FCSTD DOCUMENT  (FreeCAD 0.19R24291 (Git))
Label: front_panel
License: All rights reserved
LicenseURL: http://en.wikipedia.org/wiki/All_rights_reserved
objects: Sketcher::SketchObject×3, PartDesign::Body×1
note: 4 computed .brp shape members not serialized (recipe doc carries the construction recipe); baked Part::Feature solids carry a one-line shape summary decoded from their .brp

FEATURE [Sketcher::SketchObject] Sketch  label="Reference"
  FullyConstrained = true
  MapMode = 5
  Support = -> [XY_Plane]
  sketch-geometry (89):
    g0: Circle CenterX=-179 CenterY=-83 CenterZ=0 NormalX=0 NormalY=0 NormalZ=1 AngleXU=0 Radius=1.85
    g1: Circle CenterX=-89 CenterY=-83 CenterZ=0 NormalX=0 NormalY=0 NormalZ=1 AngleXU=0 Radius=1.85
    g2: Circle CenterX=0 CenterY=-83 CenterZ=0 NormalX=0 NormalY=0 NormalZ=1 AngleXU=0 Radius=1.85
    g3: Circle CenterX=89 CenterY=-83 CenterZ=0 NormalX=0 NormalY=0 NormalZ=1 AngleXU=0 Radius=1.85
    g4: Circle CenterX=179 CenterY=-83 CenterZ=0 NormalX=0 NormalY=0 NormalZ=1 AngleXU=0 Radius=1.85
    g5: Circle CenterX=-179 CenterY=83 CenterZ=0 NormalX=0 NormalY=0 NormalZ=1 AngleXU=0 Radius=1.85
    g6: Circle CenterX=-89 CenterY=83 CenterZ=0 NormalX=0 NormalY=0 NormalZ=1 AngleXU=0 Radius=1.85
    g7: Circle CenterX=0 CenterY=83 CenterZ=0 NormalX=0 NormalY=0 NormalZ=1 AngleXU=0 Radius=1.85
    g8: Circle CenterX=89 CenterY=83 CenterZ=0 NormalX=0 NormalY=0 NormalZ=1 AngleXU=0 Radius=1.85
    g9: Circle CenterX=179 CenterY=83 CenterZ=0 NormalX=0 NormalY=0 NormalZ=1 AngleXU=0 Radius=1.85
    g10: LineSegment StartX=-185 StartY=75.75 StartZ=0 EndX=185 EndY=75.75 EndZ=0
    g11: LineSegment StartX=185 StartY=75.75 StartZ=0 EndX=185 EndY=-75.75 EndZ=0
    g12: LineSegment StartX=185 StartY=-75.75 StartZ=0 EndX=-185 EndY=-75.75 EndZ=0
    g13: LineSegment StartX=-185 StartY=-75.75 StartZ=0 EndX=-185 EndY=75.75 EndZ=0
    g14: LineSegment StartX=-185 StartY=75.75 StartZ=0 EndX=-175 EndY=75.75 EndZ=0
    g15: LineSegment StartX=-175 StartY=75.75 StartZ=0 EndX=-175 EndY=86.75 EndZ=0
    g16: LineSegment StartX=-175 StartY=86.75 StartZ=0 EndX=-185 EndY=86.75 EndZ=0
    g17: LineSegment StartX=-185 StartY=86.75 StartZ=0 EndX=-185 EndY=75.75 EndZ=0
    g18: LineSegment StartX=-185 StartY=56.25 StartZ=0 EndX=185 EndY=56.25 EndZ=0
    g19: LineSegment StartX=-185 StartY=-56.25 StartZ=0 EndX=185 EndY=-56.25 EndZ=0
    g20: LineSegment StartX=-165.5 StartY=55.5 StartZ=0 EndX=-162.5 EndY=55.5 EndZ=0
    g21: LineSegment StartX=-162.5 StartY=55.5 StartZ=0 EndX=-162.5 EndY=-55.5 EndZ=0
    g22: LineSegment StartX=-162.5 StartY=-55.5 StartZ=0 EndX=-165.5 EndY=-55.5 EndZ=0
    g23: LineSegment StartX=-165.5 StartY=-55.5 StartZ=0 EndX=-165.5 EndY=55.5 EndZ=0
    g24: GeomPoint X=-164 Y=55.5 Z=0
    g25: LineSegment StartX=-144.5 StartY=55.5 StartZ=0 EndX=-141.5 EndY=55.5 EndZ=0
    g26: LineSegment StartX=-141.5 StartY=55.5 StartZ=0 EndX=-141.5 EndY=-55.5 EndZ=0
    g27: LineSegment StartX=-141.5 StartY=-55.5 StartZ=0 EndX=-144.5 EndY=-55.5 EndZ=0
    g28: LineSegment StartX=-144.5 StartY=-55.5 StartZ=0 EndX=-144.5 EndY=55.5 EndZ=0
    g29: LineSegment StartX=-123.5 StartY=-55.5 StartZ=0 EndX=-120.5 EndY=-55.5 EndZ=0
    g30: LineSegment StartX=-120.5 StartY=-55.5 StartZ=0 EndX=-120.5 EndY=55.5 EndZ=0
    g31: LineSegment StartX=-120.5 StartY=55.5 StartZ=0 EndX=-123.5 EndY=55.5 EndZ=0
    g32: LineSegment StartX=-123.5 StartY=55.5 StartZ=0 EndX=-123.5 EndY=-55.5 EndZ=0
    g33: LineSegment StartX=-102.5 StartY=-55.5 StartZ=0 EndX=-99.5 EndY=-55.5 EndZ=0
    g34: LineSegment StartX=-99.5 StartY=-55.5 StartZ=0 EndX=-99.5 EndY=55.5 EndZ=0
    g35: LineSegment StartX=-99.5 StartY=55.5 StartZ=0 EndX=-102.5 EndY=55.5 EndZ=0
    g36: LineSegment StartX=-102.5 StartY=55.5 StartZ=0 EndX=-102.5 EndY=-55.5 EndZ=0
    g37: LineSegment StartX=-81.5 StartY=-55.5 StartZ=0 EndX=-78.5 EndY=-55.5 EndZ=0
    g38: LineSegment StartX=-78.5 StartY=-55.5 StartZ=0 EndX=-78.5 EndY=55.5 EndZ=0
    g39: LineSegment StartX=-78.5 StartY=55.5 StartZ=0 EndX=-81.5 EndY=55.5 EndZ=0
    g40: LineSegment StartX=-81.5 StartY=55.5 StartZ=0 EndX=-81.5 EndY=-55.5 EndZ=0
    g41: LineSegment StartX=-60.5 StartY=-55.5 StartZ=0 EndX=-57.5 EndY=-55.5 EndZ=0
    g42: LineSegment StartX=-57.5 StartY=-55.5 StartZ=0 EndX=-57.5 EndY=55.5 EndZ=0
    g43: LineSegment StartX=-57.5 StartY=55.5 StartZ=0 EndX=-60.5 EndY=55.5 EndZ=0
    g44: LineSegment StartX=-60.5 StartY=55.5 StartZ=0 EndX=-60.5 EndY=-55.5 EndZ=0
    g45: LineSegment StartX=-39.5 StartY=-55.5 StartZ=0 EndX=-36.5 EndY=-55.5 EndZ=0
    g46: LineSegment StartX=-36.5 StartY=-55.5 StartZ=0 EndX=-36.5 EndY=55.5 EndZ=0
    g47: LineSegment StartX=-36.5 StartY=55.5 StartZ=0 EndX=-39.5 EndY=55.5 EndZ=0
    g48: LineSegment StartX=-39.5 StartY=55.5 StartZ=0 EndX=-39.5 EndY=-55.5 EndZ=0
    g49: LineSegment StartX=-18.5 StartY=55.5 StartZ=0 EndX=-15.5 EndY=55.5 EndZ=0
    g50: LineSegment StartX=-15.5 StartY=55.5 StartZ=0 EndX=-15.5 EndY=-55.5 EndZ=0
    g51: LineSegment StartX=-15.5 StartY=-55.5 StartZ=0 EndX=-18.5 EndY=-55.5 EndZ=0
    g52: LineSegment StartX=-18.5 StartY=-55.5 StartZ=0 EndX=-18.5 EndY=55.5 EndZ=0
    g53: LineSegment StartX=2.5 StartY=55.5 StartZ=0 EndX=5.5 EndY=55.5 EndZ=0
    g54: LineSegment StartX=5.5 StartY=55.5 StartZ=0 EndX=5.5 EndY=-55.5 EndZ=0
    g55: LineSegment StartX=5.5 StartY=-55.5 StartZ=0 EndX=2.5 EndY=-55.5 EndZ=0
    g56: LineSegment StartX=2.5 StartY=-55.5 StartZ=0 EndX=2.5 EndY=55.5 EndZ=0
    g57: LineSegment StartX=23.5 StartY=55.5 StartZ=0 EndX=26.5 EndY=55.5 EndZ=0
    g58: LineSegment StartX=26.5 StartY=55.5 StartZ=0 EndX=26.5 EndY=-55.5 EndZ=0
    g59: LineSegment StartX=26.5 StartY=-55.5 StartZ=0 EndX=23.5 EndY=-55.5 EndZ=0
    g60: LineSegment StartX=23.5 StartY=-55.5 StartZ=0 EndX=23.5 EndY=55.5 EndZ=0
    g61: LineSegment StartX=44.5 StartY=55.5 StartZ=0 EndX=47.5 EndY=55.5 EndZ=0
    g62: LineSegment StartX=47.5 StartY=55.5 StartZ=0 EndX=47.5 EndY=-55.5 EndZ=0
    g63: LineSegment StartX=47.5 StartY=-55.5 StartZ=0 EndX=44.5 EndY=-55.5 EndZ=0
    g64: LineSegment StartX=44.5 StartY=-55.5 StartZ=0 EndX=44.5 EndY=55.5 EndZ=0
    g65: LineSegment StartX=65.5 StartY=55.5 StartZ=0 EndX=68.5 EndY=55.5 EndZ=0
    g66: LineSegment StartX=68.5 StartY=55.5 StartZ=0 EndX=68.5 EndY=-55.5 EndZ=0
    g67: LineSegment StartX=68.5 StartY=-55.5 StartZ=0 EndX=65.5 EndY=-55.5 EndZ=0
    g68: LineSegment StartX=65.5 StartY=-55.5 StartZ=0 EndX=65.5 EndY=55.5 EndZ=0
    g69: LineSegment StartX=86.5 StartY=55.5 StartZ=0 EndX=89.5 EndY=55.5 EndZ=0
    g70: LineSegment StartX=89.5 StartY=55.5 StartZ=0 EndX=89.5 EndY=-55.5 EndZ=0
    g71: LineSegment StartX=89.5 StartY=-55.5 StartZ=0 EndX=86.5 EndY=-55.5 EndZ=0
    g72: LineSegment StartX=86.5 StartY=-55.5 StartZ=0 EndX=86.5 EndY=55.5 EndZ=0
    g73: LineSegment StartX=107.5 StartY=55.5 StartZ=0 EndX=110.5 EndY=55.5 EndZ=0
    g74: LineSegment StartX=110.5 StartY=55.5 StartZ=0 EndX=110.5 EndY=-55.5 EndZ=0
    g75: LineSegment StartX=110.5 StartY=-55.5 StartZ=0 EndX=107.5 EndY=-55.5 EndZ=0
    g76: LineSegment StartX=107.5 StartY=-55.5 StartZ=0 EndX=107.5 EndY=55.5 EndZ=0
    g77: LineSegment StartX=128.5 StartY=55.5 StartZ=0 EndX=131.5 EndY=55.5 EndZ=0
    g78: LineSegment StartX=131.5 StartY=55.5 StartZ=0 EndX=131.5 EndY=-55.5 EndZ=0
    g79: LineSegment StartX=131.5 StartY=-55.5 StartZ=0 EndX=128.5 EndY=-55.5 EndZ=0
    g80: LineSegment StartX=128.5 StartY=-55.5 StartZ=0 EndX=128.5 EndY=55.5 EndZ=0
    g81: LineSegment StartX=149.5 StartY=55.5 StartZ=0 EndX=152.5 EndY=55.5 EndZ=0
    g82: LineSegment StartX=152.5 StartY=55.5 StartZ=0 EndX=152.5 EndY=-55.5 EndZ=0
    g83: LineSegment StartX=152.5 StartY=-55.5 StartZ=0 EndX=149.5 EndY=-55.5 EndZ=0
    g84: LineSegment StartX=149.5 StartY=-55.5 StartZ=0 EndX=149.5 EndY=55.5 EndZ=0
    g85: LineSegment StartX=175.5 StartY=55.5 StartZ=0 EndX=178.5 EndY=55.5 EndZ=0
    g86: LineSegment StartX=178.5 StartY=55.5 StartZ=0 EndX=178.5 EndY=-55.5 EndZ=0
    g87: LineSegment StartX=178.5 StartY=-55.5 StartZ=0 EndX=175.5 EndY=-55.5 EndZ=0
    g88: LineSegment StartX=175.5 StartY=-55.5 StartZ=0 EndX=175.5 EndY=55.5 EndZ=0
  constraints (256):
    c: PointOnObject(g2,g-2)
    c: Horizontal(g0,g1)
    c: Horizontal(g1,g2)
    c: Symmetric(g1,g3,g-2)
    c: Symmetric(g0,g4,g-2)
    c: DistanceX(g1,g2) = 89
    c: DistanceX(g0,g1) = 90
    c: Equal(g0,g1)
    c: Equal(g1,g2)
    c: Equal(g2,g3)
    c: Equal(g3,g4)
    c: Diameter(g0) = 3.7
    c: Equal(g5,g6)
    c: Equal(g6,g8)
    c: Equal(g8,g9)
    c: Equal(g9,g7)
    c: Equal(g7,g0)
    c: Symmetric(g5,g0,g-1)
    c: Symmetric(g6,g1,g-1)
    c: Symmetric(g7,g2,g-1)
    c: Symmetric(g8,g3,g-1)
    c: Symmetric(g9,g4,g-1)
    c: Coincident(g10,g11)
    c: Coincident(g11,g12)
    c: Coincident(g12,g13)
    c: Coincident(g13,g10)
    c: Horizontal(g10)
    c: Horizontal(g12)
    c: Vertical(g11)
    c: Vertical(g13)
    c: DistanceY(g11,g11) = 151.5
    c: Symmetric(g10,g11,g-1)
    c: DistanceY(g10,g5) = 7.25
    c: Coincident(g14,g15)
    c: Coincident(g15,g16)
    c: Coincident(g16,g17)
    c: Coincident(g17,g14)
    c: Horizontal(g14)
    c: Horizontal(g16)
    c: Vertical(g15)
    c: Vertical(g17)
    c: Coincident(g14,g10)
    c: DistanceY(g15,g15) = 11
    c: DistanceX(g16,g16) = 10
    c: PointOnObject(g18,g13)
    c: PointOnObject(g18,g11)
    c: Horizontal(g18)
    c: PointOnObject(g19,g13)
    c: Horizontal(g19)
    c: Symmetric(g18,g19,g-1)
    c: DistanceY(g19,g18) = 112.5
    c: Coincident(g20,g21)
    c: Coincident(g21,g22)
    c: Coincident(g22,g23)
    c: Coincident(g23,g20)
    c: Horizontal(g20)
    c: Horizontal(g22)
    c: Vertical(g23)
    c: Symmetric(g20,g21,g-1)
    c: DistanceY(g23,g23) = 111
    c: DistanceX(g20,g20) = 3
    c: Symmetric(g20,g20,g24)
    c: DistanceX(g18,g24) = 21
    c: Coincident(g25,g26)
    c: Coincident(g26,g27)
    c: Coincident(g27,g28)
    c: Coincident(g28,g25)
    c: Horizontal(g25)
    c: Horizontal(g27)
    c: Vertical(g26)
    c: Vertical(g28)
    c: DistanceX(g20,g25) = 21
    c: Equal(g25,g20)
    c: Equal(g28,g23)
    c: Horizontal(g20,g25)
    c: Coincident(g29,g30)
    c: Coincident(g30,g31)
    c: Coincident(g31,g32)
    c: Coincident(g32,g29)
    c: Horizontal(g29)
    c: Horizontal(g31)
    c: Vertical(g30)
    c: Vertical(g32)
    c: Coincident(g33,g34)
    c: Coincident(g34,g35)
    c: Coincident(g35,g36)
    c: Coincident(g36,g33)
    c: Horizontal(g33)
    c: Horizontal(g35)
    c: Vertical(g34)
    c: Vertical(g36)
    c: Coincident(g37,g38)
    c: Coincident(g38,g39)
    c: Coincident(g39,g40)
    c: Coincident(g40,g37)
    c: Horizontal(g37)
    c: Horizontal(g39)
    c: Vertical(g38)
    c: Vertical(g40)
    c: Coincident(g41,g42)
    c: Coincident(g42,g43)
    c: Coincident(g43,g44)
    c: Coincident(g44,g41)
    c: Horizontal(g41)
    c: Horizontal(g43)
    c: Vertical(g42)
    c: Vertical(g44)
    c: Coincident(g45,g46)
    c: Coincident(g46,g47)
    c: Coincident(g47,g48)
    c: Coincident(g48,g45)
    c: Horizontal(g45)
    c: Horizontal(g47)
    c: Vertical(g46)
    c: Vertical(g48)
    c: Equal(g28,g30)
    c: Equal(g32,g34)
    c: Equal(g36,g38)
    c: Equal(g40,g42)
    c: Equal(g44,g46)
    c: Horizontal(g25,g31)
    c: Horizontal(g31,g35)
    c: Horizontal(g35,g39)
    c: Horizontal(g39,g43)
    c: Horizontal(g43,g47)
    c: Equal(g31,g35)
    c: Equal(g35,g39)
    c: Equal(g39,g43)
    c: Equal(g43,g47)
    c: Equal(g47,g25)
    c: DistanceX(g25,g31) = 21
    c: DistanceX(g31,g35) = 21
    c: DistanceX(g35,g39) = 21
    c: DistanceX(g39,g43) = 21
    c: DistanceX(g43,g47) = 21
    c: Coincident(g49,g50)
    c: Coincident(g50,g51)
    c: Coincident(g51,g52)
    c: Coincident(g52,g49)
    c: Horizontal(g49)
    c: Horizontal(g51)
    c: Vertical(g50)
    c: Vertical(g52)
    c: Coincident(g53,g54)
    c: Coincident(g54,g55)
    c: Coincident(g55,g56)
    c: Coincident(g56,g53)
    c: Horizontal(g53)
    c: Horizontal(g55)
    c: Vertical(g54)
    c: Vertical(g56)
    c: Coincident(g57,g58)
    c: Coincident(g58,g59)
    c: Coincident(g59,g60)
    c: Coincident(g60,g57)
    c: Horizontal(g57)
    c: Horizontal(g59)
    c: Vertical(g58)
    c: Vertical(g60)
    c: Coincident(g61,g62)
    c: Coincident(g62,g63)
    c: Coincident(g63,g64)
    c: Coincident(g64,g61)
    c: Horizontal(g61)
    c: Horizontal(g63)
    c: Vertical(g62)
    c: Vertical(g64)
    c: Coincident(g65,g66)
    c: Coincident(g66,g67)
    c: Coincident(g67,g68)
    c: Coincident(g68,g65)
    c: Horizontal(g65)
    c: Horizontal(g67)
    c: Vertical(g66)
    c: Vertical(g68)
    c: Coincident(g69,g70)
    c: Coincident(g70,g71)
    c: Coincident(g71,g72)
    c: Coincident(g72,g69)
    c: Horizontal(g69)
    c: Horizontal(g71)
    c: Vertical(g70)
    c: Vertical(g72)
    c: Coincident(g73,g74)
    c: Coincident(g74,g75)
    c: Coincident(g75,g76)
    c: Coincident(g76,g73)
    c: Horizontal(g73)
    c: Horizontal(g75)
    c: Vertical(g74)
    c: Vertical(g76)
    c: Coincident(g77,g78)
    c: Coincident(g78,g79)
    c: Coincident(g79,g80)
    c: Coincident(g80,g77)
    c: Horizontal(g77)
    c: Horizontal(g79)
    c: Vertical(g78)
    c: Vertical(g80)
    c: Coincident(g81,g82)
    c: Coincident(g82,g83)
    c: Coincident(g83,g84)
    c: Coincident(g84,g81)
    c: Horizontal(g81)
    c: Horizontal(g83)
    c: Vertical(g82)
    c: Vertical(g84)
    c: Coincident(g85,g86)
    c: Coincident(g86,g87)
    c: Coincident(g87,g88)
    c: Coincident(g88,g85)
    c: Horizontal(g85)
    c: Horizontal(g87)
    c: Vertical(g86)
    c: Vertical(g88)
    c: Equal(g52,g54)
    c: Equal(g56,g58)
    c: Equal(g60,g62)
    c: Equal(g64,g66)
    c: Equal(g68,g70)
    c: Equal(g72,g74)
    c: Equal(g76,g78)
    c: Equal(g80,g82)
    c: Equal(g84,g86)
    c: Equal(g88,g46)
    c: Horizontal(g47,g49)
    c: Horizontal(g49,g53)
    c: Horizontal(g53,g57)
    c: Horizontal(g57,g61)
    c: Horizontal(g61,g65)
    c: Horizontal(g65,g69)
    c: Horizontal(g69,g73)
    c: Horizontal(g73,g77)
    c: Horizontal(g77,g81)
    c: Horizontal(g81,g85)
    c: Equal(g47,g49)
    c: Equal(g49,g53)
    c: Equal(g53,g57)
    c: Equal(g57,g61)
    c: Equal(g61,g65)
    c: Equal(g65,g69)
    c: Equal(g69,g73)
    c: Equal(g73,g77)
    c: Equal(g77,g81)
    c: Equal(g81,g85)
    c: DistanceX(g47,g49) = 21
    c: DistanceX(g49,g53) = 21
    c: DistanceX(g57,g61) = 21
    c: DistanceX(g61,g65) = 21
    c: DistanceX(g65,g69) = 21
    c: DistanceX(g53,g57) = 21
    c: DistanceX(g69,g73) = 21
    c: DistanceX(g73,g77) = 21
    c: DistanceX(g77,g81) = 21
    c: DistanceX(g81,g85) = 26
    c: DistanceX(g12,g12) = 370
FEATURE [Sketcher::SketchObject] Sketch001  label="Displays"
  ExternalGeometry = -> [Sketch]
  FullyConstrained = true
  MapMode = 5
  Support = -> [XY_Plane]
  sketch-geometry (159):
    g0: GeomPoint X=-153.5 Y=55.5 Z=0
    g1: GeomPoint X=-111.5 Y=55.5 Z=0
    g2: GeomPoint X=-69.5 Y=55.5 Z=0
    g3: GeomPoint X=-27.5 Y=55.5 Z=0
    g4: GeomPoint X=14.5 Y=55.5 Z=0
    g5: GeomPoint X=56.5 Y=55.5 Z=0
    g6: GeomPoint X=98.5 Y=55.5 Z=0
    g7: GeomPoint X=140.5 Y=55.5 Z=0
    g8: LineSegment StartX=-167 StartY=92.5 StartZ=0 EndX=-140 EndY=92.5 EndZ=0
    g9: LineSegment StartX=-140 StartY=92.5 StartZ=0 EndX=-140 EndY=112.5 EndZ=0
    g10: LineSegment StartX=-140 StartY=112.5 StartZ=0 EndX=-167 EndY=112.5 EndZ=0
    g11: LineSegment StartX=-167 StartY=112.5 StartZ=0 EndX=-167 EndY=92.5 EndZ=0
    g12: LineSegment StartX=-165.25 StartY=114.25 StartZ=0 EndX=-141.75 EndY=114.25 EndZ=0
    g13: LineSegment StartX=-141.75 StartY=114.25 StartZ=0 EndX=-141.75 EndY=90.75 EndZ=0
    g14: LineSegment StartX=-141.75 StartY=90.75 StartZ=0 EndX=-165.25 EndY=90.75 EndZ=0
    g15: LineSegment StartX=-165.25 StartY=90.75 StartZ=0 EndX=-165.25 EndY=114.25 EndZ=0
    g16: GeomPoint X=-153.5 Y=102.5 Z=0
    g17: Circle CenterX=-165.25 CenterY=114.25 CenterZ=0 NormalX=0 NormalY=0 NormalZ=1 AngleXU=0 Radius=1.5
    g18: Circle CenterX=-141.75 CenterY=114.25 CenterZ=0 NormalX=0 NormalY=0 NormalZ=1 AngleXU=0 Radius=1.5
    g19: Circle CenterX=-141.75 CenterY=90.75 CenterZ=0 NormalX=0 NormalY=0 NormalZ=1 AngleXU=0 Radius=1.5
    g20: Circle CenterX=-165.25 CenterY=90.75 CenterZ=0 NormalX=0 NormalY=0 NormalZ=1 AngleXU=0 Radius=1.5
    g21: ArcOfCircle CenterX=-162 CenterY=90.25 CenterZ=0 NormalX=0 NormalY=0 NormalZ=1 AngleXU=0 Radius=1.25 StartAngle=1.5708 EndAngle=4.71239
    g22: ArcOfCircle CenterX=-145 CenterY=90.25 CenterZ=0 NormalX=0 NormalY=0 NormalZ=1 AngleXU=0 Radius=1.25 StartAngle=4.71239 EndAngle=7.85398
    g23: LineSegment StartX=-162 StartY=89 StartZ=0 EndX=-145 EndY=89 EndZ=0
    g24: LineSegment StartX=-162 StartY=91.5 StartZ=0 EndX=-145 EndY=91.5 EndZ=0
    g25: GeomPoint X=-153.5 Y=90.25 Z=0
    g26: LineSegment StartX=-125 StartY=92.5 StartZ=0 EndX=-98 EndY=92.5 EndZ=0
    g27: LineSegment StartX=-98 StartY=92.5 StartZ=0 EndX=-98 EndY=112.5 EndZ=0
    g28: LineSegment StartX=-98 StartY=112.5 StartZ=0 EndX=-125 EndY=112.5 EndZ=0
    g29: LineSegment StartX=-125 StartY=112.5 StartZ=0 EndX=-125 EndY=92.5 EndZ=0
    g30: LineSegment StartX=-123.25 StartY=114.25 StartZ=0 EndX=-99.75 EndY=114.25 EndZ=0
    g31: LineSegment StartX=-99.75 StartY=114.25 StartZ=0 EndX=-99.75 EndY=90.75 EndZ=0
    g32: LineSegment StartX=-99.75 StartY=90.75 StartZ=0 EndX=-123.25 EndY=90.75 EndZ=0
    g33: LineSegment StartX=-123.25 StartY=90.75 StartZ=0 EndX=-123.25 EndY=114.25 EndZ=0
    g34: GeomPoint X=-111.5 Y=102.5 Z=0
    g35: Circle CenterX=-123.25 CenterY=114.25 CenterZ=0 NormalX=0 NormalY=0 NormalZ=1 AngleXU=0 Radius=1.5
    g36: Circle CenterX=-99.75 CenterY=114.25 CenterZ=0 NormalX=0 NormalY=0 NormalZ=1 AngleXU=0 Radius=1.5
    g37: Circle CenterX=-99.75 CenterY=90.75 CenterZ=0 NormalX=0 NormalY=0 NormalZ=1 AngleXU=0 Radius=1.5
    g38: Circle CenterX=-123.25 CenterY=90.75 CenterZ=0 NormalX=0 NormalY=0 NormalZ=1 AngleXU=0 Radius=1.5
    g39: ArcOfCircle CenterX=-120 CenterY=90.25 CenterZ=0 NormalX=0 NormalY=0 NormalZ=1 AngleXU=0 Radius=1.25 StartAngle=1.5708 EndAngle=4.71239
    g40: ArcOfCircle CenterX=-103 CenterY=90.25 CenterZ=0 NormalX=0 NormalY=0 NormalZ=1 AngleXU=0 Radius=1.25 StartAngle=4.71239 EndAngle=7.85398
    g41: LineSegment StartX=-120 StartY=89 StartZ=0 EndX=-103 EndY=89 EndZ=0
    g42: LineSegment StartX=-120 StartY=91.5 StartZ=0 EndX=-103 EndY=91.5 EndZ=0
    g43: GeomPoint X=-111.5 Y=90.25 Z=0
    g44: LineSegment StartX=-83 StartY=92.5 StartZ=0 EndX=-56 EndY=92.5 EndZ=0
    g45: LineSegment StartX=-56 StartY=92.5 StartZ=0 EndX=-56 EndY=112.5 EndZ=0
    g46: LineSegment StartX=-56 StartY=112.5 StartZ=0 EndX=-83 EndY=112.5 EndZ=0
    g47: LineSegment StartX=-83 StartY=112.5 StartZ=0 EndX=-83 EndY=92.5 EndZ=0
    g48: LineSegment StartX=-81.25 StartY=114.25 StartZ=0 EndX=-57.75 EndY=114.25 EndZ=0
    g49: LineSegment StartX=-57.75 StartY=114.25 StartZ=0 EndX=-57.75 EndY=90.75 EndZ=0
    g50: LineSegment StartX=-57.75 StartY=90.75 StartZ=0 EndX=-81.25 EndY=90.75 EndZ=0
    g51: LineSegment StartX=-81.25 StartY=90.75 StartZ=0 EndX=-81.25 EndY=114.25 EndZ=0
    g52: GeomPoint X=-69.5 Y=102.5 Z=0
    g53: Circle CenterX=-81.25 CenterY=114.25 CenterZ=0 NormalX=0 NormalY=0 NormalZ=1 AngleXU=0 Radius=1.5
    g54: Circle CenterX=-57.75 CenterY=114.25 CenterZ=0 NormalX=0 NormalY=0 NormalZ=1 AngleXU=0 Radius=1.5
    g55: Circle CenterX=-57.75 CenterY=90.75 CenterZ=0 NormalX=0 NormalY=0 NormalZ=1 AngleXU=0 Radius=1.5
    g56: Circle CenterX=-81.25 CenterY=90.75 CenterZ=0 NormalX=0 NormalY=0 NormalZ=1 AngleXU=0 Radius=1.5
    g57: ArcOfCircle CenterX=-78 CenterY=90.25 CenterZ=0 NormalX=0 NormalY=0 NormalZ=1 AngleXU=0 Radius=1.25 StartAngle=1.5708 EndAngle=4.71239
    g58: ArcOfCircle CenterX=-61 CenterY=90.25 CenterZ=0 NormalX=0 NormalY=0 NormalZ=1 AngleXU=0 Radius=1.25 StartAngle=4.71239 EndAngle=7.85398
    g59: LineSegment StartX=-78 StartY=89 StartZ=0 EndX=-61 EndY=89 EndZ=0
    g60: LineSegment StartX=-78 StartY=91.5 StartZ=0 EndX=-61 EndY=91.5 EndZ=0
    g61: GeomPoint X=-69.5 Y=90.25 Z=0
    g62: LineSegment StartX=-41 StartY=92.5 StartZ=0 EndX=-14 EndY=92.5 EndZ=0
    g63: LineSegment StartX=-14 StartY=92.5 StartZ=0 EndX=-14 EndY=112.5 EndZ=0
    g64: LineSegment StartX=-14 StartY=112.5 StartZ=0 EndX=-41 EndY=112.5 EndZ=0
    g65: LineSegment StartX=-41 StartY=112.5 StartZ=0 EndX=-41 EndY=92.5 EndZ=0
    g66: LineSegment StartX=-39.25 StartY=114.25 StartZ=0 EndX=-15.75 EndY=114.25 EndZ=0
    g67: LineSegment StartX=-15.75 StartY=114.25 StartZ=0 EndX=-15.75 EndY=90.75 EndZ=0
    g68: LineSegment StartX=-15.75 StartY=90.75 StartZ=0 EndX=-39.25 EndY=90.75 EndZ=0
    g69: LineSegment StartX=-39.25 StartY=90.75 StartZ=0 EndX=-39.25 EndY=114.25 EndZ=0
    g70: GeomPoint X=-27.5 Y=102.5 Z=0
    g71: Circle CenterX=-39.25 CenterY=114.25 CenterZ=0 NormalX=0 NormalY=0 NormalZ=1 AngleXU=0 Radius=1.5
    g72: Circle CenterX=-15.75 CenterY=114.25 CenterZ=0 NormalX=0 NormalY=0 NormalZ=1 AngleXU=0 Radius=1.5
    g73: Circle CenterX=-15.75 CenterY=90.75 CenterZ=0 NormalX=0 NormalY=0 NormalZ=1 AngleXU=0 Radius=1.5
    g74: Circle CenterX=-39.25 CenterY=90.75 CenterZ=0 NormalX=0 NormalY=0 NormalZ=1 AngleXU=0 Radius=1.5
    g75: ArcOfCircle CenterX=-36 CenterY=90.25 CenterZ=0 NormalX=0 NormalY=0 NormalZ=1 AngleXU=0 Radius=1.25 StartAngle=1.5708 EndAngle=4.71239
    g76: ArcOfCircle CenterX=-19 CenterY=90.25 CenterZ=0 NormalX=0 NormalY=0 NormalZ=1 AngleXU=0 Radius=1.25 StartAngle=4.71239 EndAngle=7.85398
    g77: LineSegment StartX=-36 StartY=89 StartZ=0 EndX=-19 EndY=89 EndZ=0
    g78: LineSegment StartX=-36 StartY=91.5 StartZ=0 EndX=-19 EndY=91.5 EndZ=0
    g79: GeomPoint X=-27.5 Y=90.25 Z=0
    g80: LineSegment StartX=1 StartY=92.5 StartZ=0 EndX=28 EndY=92.5 EndZ=0
    g81: LineSegment StartX=28 StartY=92.5 StartZ=0 EndX=28 EndY=112.5 EndZ=0
    g82: LineSegment StartX=28 StartY=112.5 StartZ=0 EndX=1 EndY=112.5 EndZ=0
    g83: LineSegment StartX=1 StartY=112.5 StartZ=0 EndX=1 EndY=92.5 EndZ=0
    g84: LineSegment StartX=2.75 StartY=114.25 StartZ=0 EndX=26.25 EndY=114.25 EndZ=0
    g85: LineSegment StartX=26.25 StartY=114.25 StartZ=0 EndX=26.25 EndY=90.75 EndZ=0
    g86: LineSegment StartX=26.25 StartY=90.75 StartZ=0 EndX=2.75 EndY=90.75 EndZ=0
    g87: LineSegment StartX=2.75 StartY=90.75 StartZ=0 EndX=2.75 EndY=114.25 EndZ=0
    g88: GeomPoint X=14.5 Y=102.5 Z=0
    g89: Circle CenterX=2.75 CenterY=114.25 CenterZ=0 NormalX=0 NormalY=0 NormalZ=1 AngleXU=0 Radius=1.5
    g90: Circle CenterX=26.25 CenterY=114.25 CenterZ=0 NormalX=0 NormalY=0 NormalZ=1 AngleXU=0 Radius=1.5
    g91: Circle CenterX=26.25 CenterY=90.75 CenterZ=0 NormalX=0 NormalY=0 NormalZ=1 AngleXU=0 Radius=1.5
    g92: Circle CenterX=2.75 CenterY=90.75 CenterZ=0 NormalX=0 NormalY=0 NormalZ=1 AngleXU=0 Radius=1.5
    g93: ArcOfCircle CenterX=6 CenterY=90.25 CenterZ=0 NormalX=0 NormalY=0 NormalZ=1 AngleXU=0 Radius=1.25 StartAngle=1.5708 EndAngle=4.71239
    g94: ArcOfCircle CenterX=23 CenterY=90.25 CenterZ=0 NormalX=0 NormalY=0 NormalZ=1 AngleXU=0 Radius=1.25 StartAngle=4.71239 EndAngle=7.85398
    g95: LineSegment StartX=6 StartY=89 StartZ=0 EndX=23 EndY=89 EndZ=0
    g96: LineSegment StartX=6 StartY=91.5 StartZ=0 EndX=23 EndY=91.5 EndZ=0
    g97: GeomPoint X=14.5 Y=90.25 Z=0
    g98: LineSegment StartX=43 StartY=92.5 StartZ=0 EndX=70 EndY=92.5 EndZ=0
    g99: LineSegment StartX=70 StartY=92.5 StartZ=0 EndX=70 EndY=112.5 EndZ=0
    g100: LineSegment StartX=70 StartY=112.5 StartZ=0 EndX=43 EndY=112.5 EndZ=0
    g101: LineSegment StartX=43 StartY=112.5 StartZ=0 EndX=43 EndY=92.5 EndZ=0
    g102: LineSegment StartX=44.75 StartY=114.25 StartZ=0 EndX=68.25 EndY=114.25 EndZ=0
    g103: LineSegment StartX=68.25 StartY=114.25 StartZ=0 EndX=68.25 EndY=90.75 EndZ=0
    g104: LineSegment StartX=68.25 StartY=90.75 StartZ=0 EndX=44.75 EndY=90.75 EndZ=0
    g105: LineSegment StartX=44.75 StartY=90.75 StartZ=0 EndX=44.75 EndY=114.25 EndZ=0
    g106: GeomPoint X=56.5 Y=102.5 Z=0
    g107: Circle CenterX=44.75 CenterY=114.25 CenterZ=0 NormalX=0 NormalY=0 NormalZ=1 AngleXU=0 Radius=1.5
    g108: Circle CenterX=68.25 CenterY=114.25 CenterZ=0 NormalX=0 NormalY=0 NormalZ=1 AngleXU=0 Radius=1.5
    g109: Circle CenterX=68.25 CenterY=90.75 CenterZ=0 NormalX=0 NormalY=0 NormalZ=1 AngleXU=0 Radius=1.5
    g110: Circle CenterX=44.75 CenterY=90.75 CenterZ=0 NormalX=0 NormalY=0 NormalZ=1 AngleXU=0 Radius=1.5
    g111: ArcOfCircle CenterX=48 CenterY=90.25 CenterZ=0 NormalX=0 NormalY=0 NormalZ=1 AngleXU=0 Radius=1.25 StartAngle=1.5708 EndAngle=4.71239
    g112: ArcOfCircle CenterX=65 CenterY=90.25 CenterZ=0 NormalX=0 NormalY=0 NormalZ=1 AngleXU=0 Radius=1.25 StartAngle=4.71239 EndAngle=7.85398
    g113: LineSegment StartX=48 StartY=89 StartZ=0 EndX=65 EndY=89 EndZ=0
    g114: LineSegment StartX=48 StartY=91.5 StartZ=0 EndX=65 EndY=91.5 EndZ=0
    g115: GeomPoint X=56.5 Y=90.25 Z=0
    g116: LineSegment StartX=85 StartY=92.5 StartZ=0 EndX=112 EndY=92.5 EndZ=0
    g117: LineSegment StartX=112 StartY=92.5 StartZ=0 EndX=112 EndY=112.5 EndZ=0
    g118: LineSegment StartX=112 StartY=112.5 StartZ=0 EndX=85 EndY=112.5 EndZ=0
    g119: LineSegment StartX=85 StartY=112.5 StartZ=0 EndX=85 EndY=92.5 EndZ=0
    g120: LineSegment StartX=86.75 StartY=114.25 StartZ=0 EndX=110.25 EndY=114.25 EndZ=0
    g121: LineSegment StartX=110.25 StartY=114.25 StartZ=0 EndX=110.25 EndY=90.75 EndZ=0
    g122: LineSegment StartX=110.25 StartY=90.75 StartZ=0 EndX=86.75 EndY=90.75 EndZ=0
    g123: LineSegment StartX=86.75 StartY=90.75 StartZ=0 EndX=86.75 EndY=114.25 EndZ=0
    g124: GeomPoint X=98.5 Y=102.5 Z=0
    g125: Circle CenterX=86.75 CenterY=114.25 CenterZ=0 NormalX=0 NormalY=0 NormalZ=1 AngleXU=0 Radius=1.5
    g126: Circle CenterX=110.25 CenterY=114.25 CenterZ=0 NormalX=0 NormalY=0 NormalZ=1 AngleXU=0 Radius=1.5
    g127: Circle CenterX=110.25 CenterY=90.75 CenterZ=0 NormalX=0 NormalY=0 NormalZ=1 AngleXU=0 Radius=1.5
    g128: Circle CenterX=86.75 CenterY=90.75 CenterZ=0 NormalX=0 NormalY=0 NormalZ=1 AngleXU=0 Radius=1.5
    g129: ArcOfCircle CenterX=90 CenterY=90.25 CenterZ=0 NormalX=0 NormalY=0 NormalZ=1 AngleXU=0 Radius=1.25 StartAngle=1.5708 EndAngle=4.71239
    g130: ArcOfCircle CenterX=107 CenterY=90.25 CenterZ=0 NormalX=0 NormalY=0 NormalZ=1 AngleXU=0 Radius=1.25 StartAngle=4.71239 EndAngle=7.85398
    g131: LineSegment StartX=90 StartY=89 StartZ=0 EndX=107 EndY=89 EndZ=0
    g132: LineSegment StartX=90 StartY=91.5 StartZ=0 EndX=107 EndY=91.5 EndZ=0
    g133: GeomPoint X=98.5 Y=90.25 Z=0
    g134: LineSegment StartX=127 StartY=92.5 StartZ=0 EndX=154 EndY=92.5 EndZ=0
    g135: LineSegment StartX=154 StartY=92.5 StartZ=0 EndX=154 EndY=112.5 EndZ=0
    g136: LineSegment StartX=154 StartY=112.5 StartZ=0 EndX=127 EndY=112.5 EndZ=0
    g137: LineSegment StartX=127 StartY=112.5 StartZ=0 EndX=127 EndY=92.5 EndZ=0
    g138: LineSegment StartX=128.75 StartY=114.25 StartZ=0 EndX=152.25 EndY=114.25 EndZ=0
    g139: LineSegment StartX=152.25 StartY=114.25 StartZ=0 EndX=152.25 EndY=90.75 EndZ=0
    g140: LineSegment StartX=152.25 StartY=90.75 StartZ=0 EndX=128.75 EndY=90.75 EndZ=0
    g141: LineSegment StartX=128.75 StartY=90.75 StartZ=0 EndX=128.75 EndY=114.25 EndZ=0
    g142: GeomPoint X=140.5 Y=102.5 Z=0
    g143: Circle CenterX=128.75 CenterY=114.25 CenterZ=0 NormalX=0 NormalY=0 NormalZ=1 AngleXU=0 Radius=1.5
    g144: Circle CenterX=152.25 CenterY=114.25 CenterZ=0 NormalX=0 NormalY=0 NormalZ=1 AngleXU=0 Radius=1.5
    g145: Circle CenterX=152.25 CenterY=90.75 CenterZ=0 NormalX=0 NormalY=0 NormalZ=1 AngleXU=0 Radius=1.5
    g146: Circle CenterX=128.75 CenterY=90.75 CenterZ=0 NormalX=0 NormalY=0 NormalZ=1 AngleXU=0 Radius=1.5
    g147: ArcOfCircle CenterX=132 CenterY=90.25 CenterZ=0 NormalX=0 NormalY=0 NormalZ=1 AngleXU=0 Radius=1.25 StartAngle=1.5708 EndAngle=4.71239
    g148: ArcOfCircle CenterX=149 CenterY=90.25 CenterZ=0 NormalX=0 NormalY=0 NormalZ=1 AngleXU=0 Radius=1.25 StartAngle=4.71239 EndAngle=7.85398
    g149: LineSegment StartX=132 StartY=89 StartZ=0 EndX=149 EndY=89 EndZ=0
    g150: LineSegment StartX=132 StartY=91.5 StartZ=0 EndX=149 EndY=91.5 EndZ=0
    g151: GeomPoint X=140.5 Y=90.25 Z=0
    g152: LineSegment StartX=-141.75 StartY=114.25 StartZ=0 EndX=-123.25 EndY=114.25 EndZ=0
    g153: LineSegment StartX=-99.75 StartY=114.25 StartZ=0 EndX=-81.25 EndY=114.25 EndZ=0
    g154: LineSegment StartX=-57.75 StartY=114.25 StartZ=0 EndX=-39.25 EndY=114.25 EndZ=0
    g155: LineSegment StartX=-15.75 StartY=114.25 StartZ=0 EndX=2.75 EndY=114.25 EndZ=0
    g156: LineSegment StartX=26.25 StartY=114.25 StartZ=0 EndX=44.75 EndY=114.25 EndZ=0
    g157: LineSegment StartX=68.25 StartY=114.25 StartZ=0 EndX=86.75 EndY=114.25 EndZ=0
    g158: LineSegment StartX=110.25 StartY=114.25 StartZ=0 EndX=128.75 EndY=114.25 EndZ=0
  constraints (366):
    c: Symmetric(g-3,g-6,g0)
    c: Symmetric(g-7,g-10,g1)
    c: Symmetric(g-11,g-14,g2)
    c: Symmetric(g-15,g-18,g3)
    c: Symmetric(g-19,g-21,g4)
    c: Symmetric(g-23,g-26,g5)
    c: Symmetric(g-27,g-30,g6)
    c: Symmetric(g-31,g-34,g7)
    c: Coincident(g8,g9)
    c: Coincident(g9,g10)
    c: Coincident(g10,g11)
    c: Coincident(g11,g8)
    c: Horizontal(g8)
    c: Horizontal(g10)
    c: Vertical(g9)
    c: Vertical(g11)
    c: DistanceX(g8,g8) = 27
    c: DistanceY(g11,g11) = 20
    c: Coincident(g12,g13)
    c: Coincident(g13,g14)
    c: Coincident(g14,g15)
    c: Coincident(g15,g12)
    c: Horizontal(g12)
    c: Horizontal(g14)
    c: Vertical(g13)
    c: Vertical(g15)
    c: DistanceX(g12,g12) = 23.5
    c: DistanceY(g13,g13) = 23.5
    c: Symmetric(g14,g12,g16)
    c: Symmetric(g8,g9,g16)
    c: Coincident(g17,g12)
    c: Coincident(g18,g12)
    c: Coincident(g19,g13)
    c: Coincident(g20,g14)
    c: Equal(g20,g19)
    c: Equal(g19,g18)
    c: Equal(g18,g17)
    c: Diameter(g17) = 3
    c: Tangent(g21,g24) = 1.5708
    c: Tangent(g21,g23) = -1.5708
    c: Tangent(g23,g22) = -1.5708
    c: Tangent(g24,g22) = 1.5708
    c: Horizontal(g23)
    c: Equal(g21,g22)
    c: DistanceY(g22,g22) = 2.5
    c: Symmetric(g22,g21,g25)
    c: Vertical(g25,g16)
    c: DistanceX(g21,g22) = 17
    c: DistanceY(g22,g19) = 0.5
    c: Coincident(g26,g27)
    c: Coincident(g27,g28)
    c: Coincident(g28,g29)
    c: Coincident(g29,g26)
    c: Horizontal(g26)
    c: Horizontal(g28)
    c: Vertical(g27)
    c: Vertical(g29)
    c: Equal(g8,g26) = 27
    c: Equal(g11,g29) = 20
    c: Coincident(g30,g31)
    c: Coincident(g31,g32)
    c: Coincident(g32,g33)
    c: Coincident(g33,g30)
    c: Horizontal(g30)
    c: Horizontal(g32)
    c: Vertical(g31)
    c: Vertical(g33)
    c: Equal(g12,g30) = 23.5
    c: Equal(g13,g31) = 23.5
    c: Symmetric(g32,g30,g34)
    c: Symmetric(g26,g27,g34)
    c: Coincident(g35,g30)
    c: Coincident(g36,g30)
    c: Coincident(g37,g31)
    c: Coincident(g38,g32)
    c: Equal(g38,g37)
    c: Equal(g37,g36)
    c: Equal(g36,g35)
    c: Equal(g17,g35) = 3
    c: Tangent(g39,g42) = 1.5708
    c: Tangent(g39,g41) = -1.5708
    c: Tangent(g41,g40) = -1.5708
    c: Tangent(g42,g40) = 1.5708
    c: Horizontal(g41)
    c: Equal(g39,g40)
    c: Equal(g22,g40) = 2.5
    c: Symmetric(g40,g39,g43)
    c: Vertical(g43,g34)
    c: DistanceX(g39,g40) = 17
    c: DistanceY(g40,g37) = 0.5
    c: Coincident(g44,g45)
    c: Coincident(g45,g46)
    c: Coincident(g46,g47)
    c: Coincident(g47,g44)
    c: Horizontal(g44)
    c: Horizontal(g46)
    c: Vertical(g45)
    c: Vertical(g47)
    c: Equal(g8,g44) = 27
    c: Equal(g11,g47) = 20
    c: Coincident(g48,g49)
    c: Coincident(g49,g50)
    c: Coincident(g50,g51)
    c: Coincident(g51,g48)
    c: Horizontal(g48)
    c: Horizontal(g50)
    c: Vertical(g49)
    c: Vertical(g51)
    c: Equal(g12,g48) = 23.5
    c: Equal(g13,g49) = 23.5
    c: Symmetric(g50,g48,g52)
    c: Symmetric(g44,g45,g52)
    c: Coincident(g53,g48)
    c: Coincident(g54,g48)
    c: Coincident(g55,g49)
    c: Coincident(g56,g50)
    c: Equal(g56,g55)
    c: Equal(g55,g54)
    c: Equal(g54,g53)
    c: Equal(g17,g53) = 3
    c: Tangent(g57,g60) = 1.5708
    c: Tangent(g57,g59) = -1.5708
    c: Tangent(g59,g58) = -1.5708
    c: Tangent(g60,g58) = 1.5708
    c: Horizontal(g59)
    c: Equal(g57,g58)
    c: Equal(g22,g58) = 2.5
    c: Symmetric(g58,g57,g61)
    c: Vertical(g61,g52)
    c: DistanceX(g57,g58) = 17
    c: DistanceY(g58,g55) = 0.5
    c: Coincident(g62,g63)
    c: Coincident(g63,g64)
    c: Coincident(g64,g65)
    c: Coincident(g65,g62)
    c: Horizontal(g62)
    c: Horizontal(g64)
    c: Vertical(g63)
    c: Vertical(g65)
    c: Equal(g8,g62) = 27
    c: Equal(g11,g65) = 20
    c: Coincident(g66,g67)
    c: Coincident(g67,g68)
    c: Coincident(g68,g69)
    c: Coincident(g69,g66)
    c: Horizontal(g66)
    c: Horizontal(g68)
    c: Vertical(g67)
    c: Vertical(g69)
    c: Equal(g12,g66) = 23.5
    c: Equal(g13,g67) = 23.5
    c: Symmetric(g68,g66,g70)
    c: Symmetric(g62,g63,g70)
    c: Coincident(g71,g66)
    c: Coincident(g72,g66)
    c: Coincident(g73,g67)
    c: Coincident(g74,g68)
    c: Equal(g74,g73)
    c: Equal(g73,g72)
    c: Equal(g72,g71)
    c: Equal(g17,g71) = 3
    c: Tangent(g75,g78) = 1.5708
    c: Tangent(g75,g77) = -1.5708
    c: Tangent(g77,g76) = -1.5708
    c: Tangent(g78,g76) = 1.5708
    c: Horizontal(g77)
    c: Equal(g75,g76)
    c: Equal(g22,g76) = 2.5
    c: Symmetric(g76,g75,g79)
    c: Vertical(g79,g70)
    c: DistanceX(g75,g76) = 17
    c: DistanceY(g76,g73) = 0.5
    c: Coincident(g80,g81)
    c: Coincident(g81,g82)
    c: Coincident(g82,g83)
    c: Coincident(g83,g80)
    c: Horizontal(g80)
    c: Horizontal(g82)
    c: Vertical(g81)
    c: Vertical(g83)
    c: Equal(g8,g80) = 27
    c: Equal(g11,g83) = 20
    c: Coincident(g84,g85)
    c: Coincident(g85,g86)
    c: Coincident(g86,g87)
    c: Coincident(g87,g84)
    c: Horizontal(g84)
    c: Horizontal(g86)
    c: Vertical(g85)
    c: Vertical(g87)
    c: Equal(g12,g84) = 23.5
    c: Equal(g13,g85) = 23.5
    c: Symmetric(g86,g84,g88)
    c: Symmetric(g80,g81,g88)
    c: Coincident(g89,g84)
    c: Coincident(g90,g84)
    c: Coincident(g91,g85)
    c: Coincident(g92,g86)
    c: Equal(g92,g91)
    c: Equal(g91,g90)
    c: Equal(g90,g89)
    c: Equal(g17,g89) = 3
    c: Tangent(g93,g96) = 1.5708
    c: Tangent(g93,g95) = -1.5708
    c: Tangent(g95,g94) = -1.5708
    c: Tangent(g96,g94) = 1.5708
    c: Horizontal(g95)
    c: Equal(g93,g94)
    c: Equal(g22,g94) = 2.5
    c: Symmetric(g94,g93,g97)
    c: Vertical(g97,g88)
    c: DistanceX(g93,g94) = 17
    c: DistanceY(g94,g91) = 0.5
    c: Coincident(g98,g99)
    c: Coincident(g99,g100)
    c: Coincident(g100,g101)
    c: Coincident(g101,g98)
    c: Horizontal(g98)
    c: Horizontal(g100)
    c: Vertical(g99)
    c: Vertical(g101)
    c: Equal(g8,g98) = 27
    c: Equal(g11,g101) = 20
    c: Coincident(g102,g103)
    c: Coincident(g103,g104)
    c: Coincident(g104,g105)
    c: Coincident(g105,g102)
    c: Horizontal(g102)
    c: Horizontal(g104)
    c: Vertical(g103)
    c: Vertical(g105)
    c: Equal(g12,g102) = 23.5
    c: Equal(g13,g103) = 23.5
    c: Symmetric(g104,g102,g106)
    c: Symmetric(g98,g99,g106)
    c: Coincident(g107,g102)
    c: Coincident(g108,g102)
    c: Coincident(g109,g103)
    c: Coincident(g110,g104)
    c: Equal(g110,g109)
    c: Equal(g109,g108)
    c: Equal(g108,g107)
    c: Equal(g17,g107) = 3
    c: Tangent(g111,g114) = 1.5708
    c: Tangent(g111,g113) = -1.5708
    c: Tangent(g113,g112) = -1.5708
    c: Tangent(g114,g112) = 1.5708
    c: Horizontal(g113)
    c: Equal(g111,g112)
    c: Equal(g22,g112) = 2.5
    c: Symmetric(g112,g111,g115)
    c: Vertical(g115,g106)
    c: DistanceX(g111,g112) = 17
    c: DistanceY(g112,g109) = 0.5
    c: Coincident(g116,g117)
    c: Coincident(g117,g118)
    c: Coincident(g118,g119)
    c: Coincident(g119,g116)
    c: Horizontal(g116)
    c: Horizontal(g118)
    c: Vertical(g117)
    c: Vertical(g119)
    c: Equal(g8,g116) = 27
    c: Equal(g11,g119) = 20
    c: Coincident(g120,g121)
    c: Coincident(g121,g122)
    c: Coincident(g122,g123)
    c: Coincident(g123,g120)
    c: Horizontal(g120)
    c: Horizontal(g122)
    c: Vertical(g121)
    c: Vertical(g123)
    c: Equal(g12,g120) = 23.5
    c: Equal(g13,g121) = 23.5
    c: Symmetric(g122,g120,g124)
    c: Symmetric(g116,g117,g124)
    c: Coincident(g125,g120)
    c: Coincident(g126,g120)
    c: Coincident(g127,g121)
    c: Coincident(g128,g122)
    c: Equal(g128,g127)
    c: Equal(g127,g126)
    c: Equal(g126,g125)
    c: Equal(g17,g125) = 3
    c: Tangent(g129,g132) = 1.5708
    c: Tangent(g129,g131) = -1.5708
    c: Tangent(g131,g130) = -1.5708
    c: Tangent(g132,g130) = 1.5708
    c: Horizontal(g131)
    c: Equal(g129,g130)
    c: Equal(g22,g130) = 2.5
    c: Symmetric(g130,g129,g133)
    c: Vertical(g133,g124)
    c: DistanceX(g129,g130) = 17
    c: DistanceY(g130,g127) = 0.5
    c: Coincident(g134,g135)
    c: Coincident(g135,g136)
    c: Coincident(g136,g137)
    c: Coincident(g137,g134)
    c: Horizontal(g134)
    c: Horizontal(g136)
    c: Vertical(g135)
    c: Vertical(g137)
    c: Equal(g8,g134) = 27
    c: Equal(g11,g137) = 20
    c: Coincident(g138,g139)
    c: Coincident(g139,g140)
    c: Coincident(g140,g141)
    c: Coincident(g141,g138)
    c: Horizontal(g138)
    c: Horizontal(g140)
    c: Vertical(g139)
    c: Vertical(g141)
    c: Equal(g12,g138) = 23.5
    c: Equal(g13,g139) = 23.5
    c: Symmetric(g140,g138,g142)
    c: Symmetric(g134,g135,g142)
    c: Coincident(g143,g138)
    c: Coincident(g144,g138)
    c: Coincident(g145,g139)
    c: Coincident(g146,g140)
    c: Equal(g146,g145)
    c: Equal(g145,g144)
    c: Equal(g144,g143)
    c: Equal(g17,g143) = 3
    c: Tangent(g147,g150) = 1.5708
    c: Tangent(g147,g149) = -1.5708
    c: Tangent(g149,g148) = -1.5708
    c: Tangent(g150,g148) = 1.5708
    c: Horizontal(g149)
    c: Equal(g147,g148)
    c: Equal(g22,g148) = 2.5
    c: Symmetric(g148,g147,g151)
    c: Vertical(g151,g142)
    c: DistanceX(g147,g148) = 17
    c: DistanceY(g148,g145) = 0.5
    c: Horizontal(g18,g36)
    c: Horizontal(g36,g54)
    c: Horizontal(g54,g72)
    c: Horizontal(g72,g90)
    c: Horizontal(g90,g108)
    c: Horizontal(g108,g126)
    c: Horizontal(g126,g144)
    c: Coincident(g152,g18)
    c: Coincident(g152,g35)
    c: Coincident(g153,g36)
    c: Coincident(g153,g53)
    c: Coincident(g154,g54)
    c: Coincident(g154,g71)
    c: Coincident(g155,g72)
    c: Coincident(g155,g89)
    c: Coincident(g156,g90)
    c: Coincident(g156,g107)
    c: Coincident(g157,g108)
    c: Coincident(g157,g125)
    c: Coincident(g158,g126)
    c: Coincident(g158,g143)
    c: Equal(g158,g157)
    c: Equal(g157,g156)
    c: Equal(g156,g155)
    c: Equal(g155,g154)
    c: Equal(g154,g153)
    c: Equal(g153,g152)
    c: DistanceX(g17,g35) = 42
    c: Vertical(g0,g16)
    c: DistanceY(g-42,g20) = 4
FEATURE [Sketcher::SketchObject] Sketch002  label="Faders and Mounting"
  ExternalGeometry = -> [Sketch]
  FullyConstrained = true
  MapMode = 5
  Support = -> [XY_Plane]
  sketch-geometry (90):
    g0: LineSegment StartX=-165.5 StartY=55.5 StartZ=0 EndX=-162.5 EndY=55.5 EndZ=0
    g1: LineSegment StartX=-162.5 StartY=55.5 StartZ=0 EndX=-162.5 EndY=-55.5 EndZ=0
    g2: LineSegment StartX=-162.5 StartY=-55.5 StartZ=0 EndX=-165.5 EndY=-55.5 EndZ=0
    g3: LineSegment StartX=-165.5 StartY=-55.5 StartZ=0 EndX=-165.5 EndY=55.5 EndZ=0
    g4: LineSegment StartX=-144.5 StartY=55.5 StartZ=0 EndX=-141.5 EndY=55.5 EndZ=0
    g5: LineSegment StartX=-141.5 StartY=55.5 StartZ=0 EndX=-141.5 EndY=-55.5 EndZ=0
    g6: LineSegment StartX=-141.5 StartY=-55.5 StartZ=0 EndX=-144.5 EndY=-55.5 EndZ=0
    g7: LineSegment StartX=-144.5 StartY=-55.5 StartZ=0 EndX=-144.5 EndY=55.5 EndZ=0
    g8: LineSegment StartX=-123.5 StartY=55.5 StartZ=0 EndX=-120.5 EndY=55.5 EndZ=0
    g9: LineSegment StartX=-120.5 StartY=55.5 StartZ=0 EndX=-120.5 EndY=-55.5 EndZ=0
    g10: LineSegment StartX=-120.5 StartY=-55.5 StartZ=0 EndX=-123.5 EndY=-55.5 EndZ=0
    g11: LineSegment StartX=-123.5 StartY=-55.5 StartZ=0 EndX=-123.5 EndY=55.5 EndZ=0
    g12: LineSegment StartX=-102.5 StartY=55.5 StartZ=0 EndX=-99.5 EndY=55.5 EndZ=0
    g13: LineSegment StartX=-99.5 StartY=55.5 StartZ=0 EndX=-99.5 EndY=-55.5 EndZ=0
    g14: LineSegment StartX=-99.5 StartY=-55.5 StartZ=0 EndX=-102.5 EndY=-55.5 EndZ=0
    g15: LineSegment StartX=-102.5 StartY=-55.5 StartZ=0 EndX=-102.5 EndY=55.5 EndZ=0
    g16: LineSegment StartX=-81.5 StartY=55.5 StartZ=0 EndX=-78.5 EndY=55.5 EndZ=0
    g17: LineSegment StartX=-78.5 StartY=55.5 StartZ=0 EndX=-78.5 EndY=-55.5 EndZ=0
    g18: LineSegment StartX=-78.5 StartY=-55.5 StartZ=0 EndX=-81.5 EndY=-55.5 EndZ=0
    g19: LineSegment StartX=-81.5 StartY=-55.5 StartZ=0 EndX=-81.5 EndY=55.5 EndZ=0
    g20: LineSegment StartX=-60.5 StartY=55.5 StartZ=0 EndX=-57.5 EndY=55.5 EndZ=0
    g21: LineSegment StartX=-57.5 StartY=55.5 StartZ=0 EndX=-57.5 EndY=-55.5 EndZ=0
    g22: LineSegment StartX=-57.5 StartY=-55.5 StartZ=0 EndX=-60.5 EndY=-55.5 EndZ=0
    g23: LineSegment StartX=-60.5 StartY=-55.5 StartZ=0 EndX=-60.5 EndY=55.5 EndZ=0
    g24: LineSegment StartX=-39.5 StartY=55.5 StartZ=0 EndX=-36.5 EndY=55.5 EndZ=0
    g25: LineSegment StartX=-36.5 StartY=55.5 StartZ=0 EndX=-36.5 EndY=-55.5 EndZ=0
    g26: LineSegment StartX=-36.5 StartY=-55.5 StartZ=0 EndX=-39.5 EndY=-55.5 EndZ=0
    g27: LineSegment StartX=-39.5 StartY=-55.5 StartZ=0 EndX=-39.5 EndY=55.5 EndZ=0
    g28: LineSegment StartX=-18.5 StartY=55.5 StartZ=0 EndX=-15.5 EndY=55.5 EndZ=0
    g29: LineSegment StartX=-15.5 StartY=55.5 StartZ=0 EndX=-15.5 EndY=-55.5 EndZ=0
    g30: LineSegment StartX=-15.5 StartY=-55.5 StartZ=0 EndX=-18.5 EndY=-55.5 EndZ=0
    g31: LineSegment StartX=-18.5 StartY=-55.5 StartZ=0 EndX=-18.5 EndY=55.5 EndZ=0
    g32: LineSegment StartX=2.5 StartY=55.5 StartZ=0 EndX=5.5 EndY=55.5 EndZ=0
    g33: LineSegment StartX=5.5 StartY=55.5 StartZ=0 EndX=5.5 EndY=-55.5 EndZ=0
    g34: LineSegment StartX=5.5 StartY=-55.5 StartZ=0 EndX=2.5 EndY=-55.5 EndZ=0
    g35: LineSegment StartX=2.5 StartY=-55.5 StartZ=0 EndX=2.5 EndY=55.5 EndZ=0
    g36: LineSegment StartX=23.5 StartY=55.5 StartZ=0 EndX=26.5 EndY=55.5 EndZ=0
    g37: LineSegment StartX=26.5 StartY=55.5 StartZ=0 EndX=26.5 EndY=-55.5 EndZ=0
    g38: LineSegment StartX=26.5 StartY=-55.5 StartZ=0 EndX=23.5 EndY=-55.5 EndZ=0
    g39: LineSegment StartX=23.5 StartY=-55.5 StartZ=0 EndX=23.5 EndY=55.5 EndZ=0
    g40: LineSegment StartX=44.5 StartY=55.5 StartZ=0 EndX=47.5 EndY=55.5 EndZ=0
    g41: LineSegment StartX=47.5 StartY=55.5 StartZ=0 EndX=47.5 EndY=-55.5 EndZ=0
    g42: LineSegment StartX=47.5 StartY=-55.5 StartZ=0 EndX=44.5 EndY=-55.5 EndZ=0
    g43: LineSegment StartX=44.5 StartY=-55.5 StartZ=0 EndX=44.5 EndY=55.5 EndZ=0
    g44: LineSegment StartX=65.5 StartY=55.5 StartZ=0 EndX=68.5 EndY=55.5 EndZ=0
    g45: LineSegment StartX=68.5 StartY=55.5 StartZ=0 EndX=68.5 EndY=-55.5 EndZ=0
    g46: LineSegment StartX=68.5 StartY=-55.5 StartZ=0 EndX=65.5 EndY=-55.5 EndZ=0
    g47: LineSegment StartX=65.5 StartY=-55.5 StartZ=0 EndX=65.5 EndY=55.5 EndZ=0
    g48: LineSegment StartX=86.5 StartY=55.5 StartZ=0 EndX=89.5 EndY=55.5 EndZ=0
    g49: LineSegment StartX=89.5 StartY=55.5 StartZ=0 EndX=89.5 EndY=-55.5 EndZ=0
    g50: LineSegment StartX=89.5 StartY=-55.5 StartZ=0 EndX=86.5 EndY=-55.5 EndZ=0
    g51: LineSegment StartX=86.5 StartY=-55.5 StartZ=0 EndX=86.5 EndY=55.5 EndZ=0
    g52: LineSegment StartX=107.5 StartY=55.5 StartZ=0 EndX=110.5 EndY=55.5 EndZ=0
    g53: LineSegment StartX=110.5 StartY=55.5 StartZ=0 EndX=110.5 EndY=-55.5 EndZ=0
    g54: LineSegment StartX=110.5 StartY=-55.5 StartZ=0 EndX=107.5 EndY=-55.5 EndZ=0
    g55: LineSegment StartX=107.5 StartY=-55.5 StartZ=0 EndX=107.5 EndY=55.5 EndZ=0
    g56: LineSegment StartX=128.5 StartY=55.5 StartZ=0 EndX=131.5 EndY=55.5 EndZ=0
    g57: LineSegment StartX=131.5 StartY=55.5 StartZ=0 EndX=131.5 EndY=-55.5 EndZ=0
    g58: LineSegment StartX=131.5 StartY=-55.5 StartZ=0 EndX=128.5 EndY=-55.5 EndZ=0
    g59: LineSegment StartX=128.5 StartY=-55.5 StartZ=0 EndX=128.5 EndY=55.5 EndZ=0
    g60: LineSegment StartX=149.5 StartY=55.5 StartZ=0 EndX=152.5 EndY=55.5 EndZ=0
    g61: LineSegment StartX=152.5 StartY=55.5 StartZ=0 EndX=152.5 EndY=-55.5 EndZ=0
    g62: LineSegment StartX=152.5 StartY=-55.5 StartZ=0 EndX=149.5 EndY=-55.5 EndZ=0
    g63: LineSegment StartX=149.5 StartY=-55.5 StartZ=0 EndX=149.5 EndY=55.5 EndZ=0
    g64: LineSegment StartX=175.5 StartY=55.5 StartZ=0 EndX=178.5 EndY=55.5 EndZ=0
    g65: LineSegment StartX=178.5 StartY=55.5 StartZ=0 EndX=178.5 EndY=-55.5 EndZ=0
    g66: LineSegment StartX=178.5 StartY=-55.5 StartZ=0 EndX=175.5 EndY=-55.5 EndZ=0
    g67: LineSegment StartX=175.5 StartY=-55.5 StartZ=0 EndX=175.5 EndY=55.5 EndZ=0
    g68: Circle CenterX=-179 CenterY=83 CenterZ=0 NormalX=0 NormalY=0 NormalZ=1 AngleXU=0 Radius=1.85
    g69: Circle CenterX=-89 CenterY=83 CenterZ=0 NormalX=0 NormalY=0 NormalZ=1 AngleXU=0 Radius=1.85
    g70: Circle CenterX=0 CenterY=83 CenterZ=0 NormalX=0 NormalY=0 NormalZ=1 AngleXU=0 Radius=1.85
    g71: Circle CenterX=89 CenterY=83 CenterZ=0 NormalX=0 NormalY=0 NormalZ=1 AngleXU=0 Radius=1.85
    g72: Circle CenterX=179 CenterY=83 CenterZ=0 NormalX=0 NormalY=0 NormalZ=1 AngleXU=0 Radius=1.85
    g73: Circle CenterX=179 CenterY=-83 CenterZ=0 NormalX=0 NormalY=0 NormalZ=1 AngleXU=0 Radius=1.85
    g74: Circle CenterX=89 CenterY=-83 CenterZ=0 NormalX=0 NormalY=0 NormalZ=1 AngleXU=0 Radius=1.85
    g75: Circle CenterX=0 CenterY=-83 CenterZ=0 NormalX=0 NormalY=0 NormalZ=1 AngleXU=0 Radius=1.85
    g76: Circle CenterX=-89 CenterY=-83 CenterZ=0 NormalX=0 NormalY=0 NormalZ=1 AngleXU=0 Radius=1.85
    g77: Circle CenterX=-179 CenterY=-83 CenterZ=0 NormalX=0 NormalY=0 NormalZ=1 AngleXU=0 Radius=1.85
    g78: LineSegment StartX=-190 StartY=150 StartZ=0 EndX=190 EndY=150 EndZ=0
    g79: LineSegment StartX=190 StartY=150 StartZ=0 EndX=190 EndY=-88 EndZ=0
    g80: LineSegment StartX=190 StartY=-88 StartZ=0 EndX=-190 EndY=-88 EndZ=0
    g81: LineSegment StartX=-190 StartY=-88 StartZ=0 EndX=-190 EndY=150 EndZ=0
    g82: LineSegment StartX=-173.5 StartY=148 StartZ=0 EndX=186.5 EndY=148 EndZ=0
    g83: LineSegment StartX=-173.5 StartY=123 StartZ=0 EndX=186.5 EndY=123 EndZ=0
    g84: Circle CenterX=-170.5 CenterY=145 CenterZ=0 NormalX=0 NormalY=0 NormalZ=1 AngleXU=0 Radius=2
    g85: Circle CenterX=183.5 CenterY=120 CenterZ=0 NormalX=0 NormalY=0 NormalZ=1 AngleXU=0 Radius=2
    g86: GeomPoint X=-164 Y=55.5 Z=0
    g87: GeomPoint X=-173.5 Y=55.5 Z=0
    g88: GeomPoint X=177 Y=55.5 Z=0
    g89: GeomPoint X=186 Y=55.5 Z=0
  constraints (221):
    c: Coincident(g0,g1)
    c: Coincident(g1,g2)
    c: Coincident(g2,g3)
    c: Coincident(g3,g0)
    c: Horizontal(g0)
    c: Horizontal(g2)
    c: Vertical(g1)
    c: Vertical(g3)
    c: Coincident(g0,g-4)
    c: Coincident(g1,g-3)
    c: Coincident(g4,g5)
    c: Coincident(g5,g6)
    c: Coincident(g6,g7)
    c: Coincident(g7,g4)
    c: Horizontal(g4)
    c: Horizontal(g6)
    c: Vertical(g5)
    c: Vertical(g7)
    c: Coincident(g4,g-5)
    c: Coincident(g5,g-6)
    c: Coincident(g8,g9)
    c: Coincident(g9,g10)
    c: Coincident(g10,g11)
    c: Coincident(g11,g8)
    c: Horizontal(g8)
    c: Horizontal(g10)
    c: Vertical(g9)
    c: Vertical(g11)
    c: Coincident(g8,g-7)
    c: Coincident(g9,g-8)
    c: Coincident(g12,g13)
    c: Coincident(g13,g14)
    c: Coincident(g14,g15)
    c: Coincident(g15,g12)
    c: Horizontal(g12)
    c: Horizontal(g14)
    c: Vertical(g13)
    c: Vertical(g15)
    c: Coincident(g12,g-9)
    c: Coincident(g13,g-10)
    c: Coincident(g16,g17)
    c: Coincident(g17,g18)
    c: Coincident(g18,g19)
    c: Coincident(g19,g16)
    c: Horizontal(g16)
    c: Horizontal(g18)
    c: Vertical(g17)
    c: Vertical(g19)
    c: Coincident(g16,g-11)
    c: Coincident(g17,g-12)
    c: Coincident(g20,g21)
    c: Coincident(g21,g22)
    c: Coincident(g22,g23)
    c: Coincident(g23,g20)
    c: Horizontal(g20)
    c: Horizontal(g22)
    c: Vertical(g21)
    c: Vertical(g23)
    c: Coincident(g20,g-13)
    c: Coincident(g21,g-14)
    c: Coincident(g24,g25)
    c: Coincident(g25,g26)
    c: Coincident(g26,g27)
    c: Coincident(g27,g24)
    c: Horizontal(g24)
    c: Horizontal(g26)
    c: Vertical(g25)
    c: Vertical(g27)
    c: Coincident(g24,g-15)
    c: Coincident(g25,g-16)
    c: Coincident(g28,g29)
    c: Coincident(g29,g30)
    c: Coincident(g30,g31)
    c: Coincident(g31,g28)
    c: Horizontal(g28)
    c: Horizontal(g30)
    c: Vertical(g29)
    c: Vertical(g31)
    c: Coincident(g28,g-17)
    c: Coincident(g29,g-18)
    c: Coincident(g32,g33)
    c: Coincident(g33,g34)
    c: Coincident(g34,g35)
    c: Coincident(g35,g32)
    c: Horizontal(g32)
    c: Horizontal(g34)
    c: Vertical(g33)
    c: Vertical(g35)
    c: Coincident(g32,g-19)
    c: Coincident(g33,g-20)
    c: Coincident(g36,g37)
    c: Coincident(g37,g38)
    c: Coincident(g38,g39)
    c: Coincident(g39,g36)
    c: Horizontal(g36)
    c: Horizontal(g38)
    c: Vertical(g37)
    c: Vertical(g39)
    c: Coincident(g36,g-21)
    c: Coincident(g37,g-22)
    c: Coincident(g40,g41)
    c: Coincident(g41,g42)
    c: Coincident(g42,g43)
    c: Coincident(g43,g40)
    c: Horizontal(g40)
    c: Horizontal(g42)
    c: Vertical(g41)
    c: Vertical(g43)
    c: Coincident(g40,g-23)
    c: Coincident(g41,g-24)
    c: Coincident(g44,g45)
    c: Coincident(g45,g46)
    c: Coincident(g46,g47)
    c: Coincident(g47,g44)
    c: Horizontal(g44)
    c: Horizontal(g46)
    c: Vertical(g45)
    c: Vertical(g47)
    c: Coincident(g44,g-25)
    c: Coincident(g45,g-26)
    c: Coincident(g48,g49)
    c: Coincident(g49,g50)
    c: Coincident(g50,g51)
    c: Coincident(g51,g48)
    c: Horizontal(g48)
    c: Horizontal(g50)
    c: Vertical(g49)
    c: Vertical(g51)
    c: Coincident(g48,g-27)
    c: Coincident(g49,g-28)
    c: Coincident(g52,g53)
    c: Coincident(g53,g54)
    c: Coincident(g54,g55)
    c: Coincident(g55,g52)
    c: Horizontal(g52)
    c: Horizontal(g54)
    c: Vertical(g53)
    c: Vertical(g55)
    c: Coincident(g52,g-29)
    c: Coincident(g53,g-30)
    c: Coincident(g56,g57)
    c: Coincident(g57,g58)
    c: Coincident(g58,g59)
    c: Coincident(g59,g56)
    c: Horizontal(g56)
    c: Horizontal(g58)
    c: Vertical(g57)
    c: Vertical(g59)
    c: Coincident(g56,g-31)
    c: Coincident(g57,g-32)
    c: Coincident(g60,g61)
    c: Coincident(g61,g62)
    c: Coincident(g62,g63)
    c: Coincident(g63,g60)
    c: Horizontal(g60)
    c: Horizontal(g62)
    c: Vertical(g61)
    c: Vertical(g63)
    c: Coincident(g60,g-33)
    c: Coincident(g61,g-34)
    c: Coincident(g64,g65)
    c: Coincident(g65,g66)
    c: Coincident(g66,g67)
    c: Coincident(g67,g64)
    c: Horizontal(g64)
    c: Horizontal(g66)
    c: Vertical(g65)
    c: Vertical(g67)
    c: Coincident(g64,g-35)
    c: Coincident(g65,g-36)
    c: Coincident(g69,g-38)
    c: Coincident(g70,g-39)
    c: Coincident(g71,g-40)
    c: Coincident(g72,g-41)
    c: Coincident(g73,g-47)
    c: Coincident(g74,g-46)
    c: Coincident(g75,g-45)
    c: PointOnObject(g-44,g75)
    c: Coincident(g76,g-43)
    c: Coincident(g77,g-42)
    c: Equal(g74,g77)
    c: Equal(g77,g73)
    c: Equal(g73,g76)
    c: Equal(g76,g68)
    c: Equal(g68,g69)
    c: Equal(g69,g70)
    c: Equal(g70,g71)
    c: Equal(g71,g72)
    c: Equal(g72,g75)
    c: Coincident(g68,g-37)
    c: Coincident(g78,g79)
    c: Coincident(g79,g80)
    c: Coincident(g80,g81)
    c: Coincident(g81,g78)
    c: Horizontal(g80)
    c: Vertical(g79)
    c: Vertical(g81)
    c: Symmetric(g78,g78,g-2)
    c: DistanceX(g80,g80) = 380
    c: DistanceY(g79,g73) = 5
    c: Horizontal(g82)
    c: DistanceX(g82,g82) = 360
    c: Horizontal(g83)
    c: Vertical(g83,g82)
    c: Vertical(g83,g82)
    c: DistanceY(g83,g82) = 25
    c: DistanceX(g82,g84) = 3
    c: DistanceX(g85,g83) = 3
    c: DistanceY(g85,g83) = 3
    c: DistanceY(g84,g82) = 3
    c: Diameter(g85) = 4
    c: Diameter(g84) = 4
    c: Symmetric(g0,g0,g86)
    c: DistanceX(g87,g86) = 9.5
    c: Horizontal(g86,g87)
    c: Vertical(g87,g83)
    c: Symmetric(g64,g64,g88)
    c: Horizontal(g89,g88)
    c: DistanceX(g88,g89) = 9
    c: DistanceY(g84,g78) = 5
    c: DistanceY(g64,g83) = 67.5
FEATURE [PartDesign::Body] Body
  Group = -> [Sketch,Sketch001,Sketch002]
  Origin = -> Origin
